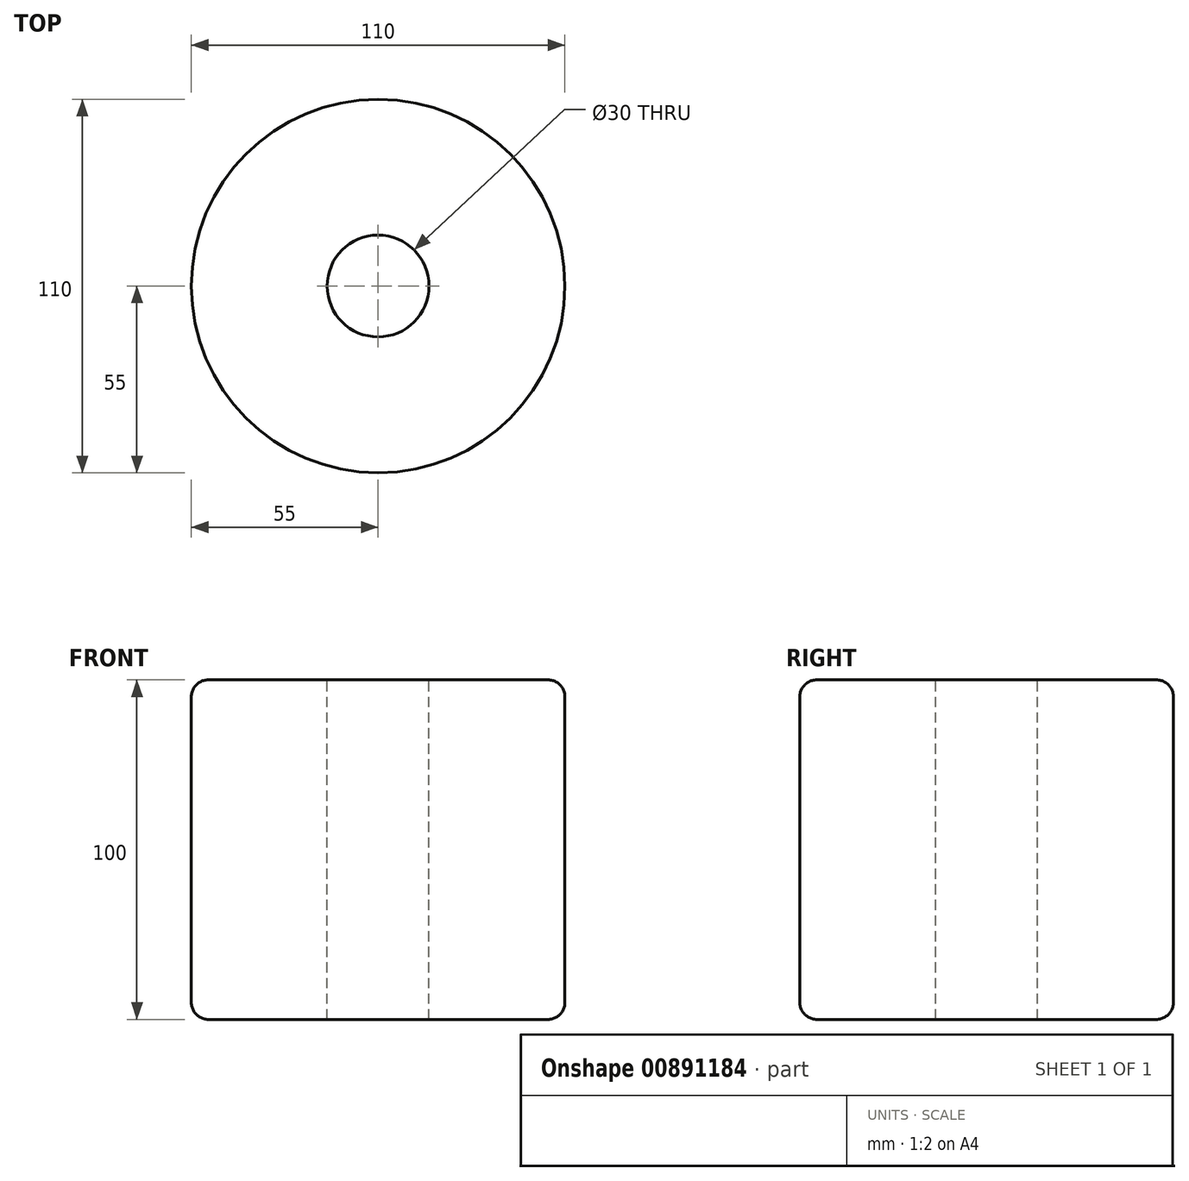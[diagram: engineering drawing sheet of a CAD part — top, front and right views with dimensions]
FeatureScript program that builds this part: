
annotation { "Feature Type Name" : "Feature", "Feature Type Description" : "" }
export const myFeature = defineFeature(function(context is Context, id is Id, definition is map)
    precondition{}
    {
        {
            var Q0;
            Q0=qCreatedBy(makeId("Front.planeOp"),FACE);
            var sketch = newSketch(context, id + "F0", { "sketchPlane" : qUnion([Q0])});
            skLineSegment(sketch, "E0", {"start": v(0, 66.21) * mm, "end": v(0, -56.82) * mm, "construction": true});
            skLineSegment(sketch, "E1.bottom", {"start": v(15, 50) * mm, "end": v(55, 50) * mm});
            skLineSegment(sketch, "E1.top", {"start": v(15, -50) * mm, "end": v(55, -50) * mm});
            skLineSegment(sketch, "E1.left", {"start": v(15, 50) * mm, "end": v(15, -50) * mm});
            skLineSegment(sketch, "E1.right", {"start": v(55, 50) * mm, "end": v(55, -50) * mm});
            skLineSegment(sketch, "E2", {"start": v(-74.72, 0) * mm, "end": v(76.46, 0) * mm, "construction": true});
            skSolve(sketch);
        }
        {
            var Q0;
            Q0=makeQuery(id+"F0.imprint","IMPRINT",FACE,{"disambiguationData":[TD([[makeQuery(id+"F0.imprint","IMPRINT",EDGE,{"derivedFrom":sQuery(id+"F0.wireOp",EDGE,"E1.bottom")}),-1.0]])]});
            var Q1;
            Q1=sQuery(id+"F0.wireOp",EDGE,"E0");
            revolve(context, id + "F1", {"surfaceOperationType" : NewSurfaceOperationType.NEW, "entities" : qUnion([Q0]), "axis" : qUnion([Q1]), "revolveType" : RevolveType.FULL});
        }
        {
            var Q0;
            Q0=makeQuery(id+"F1.opRevolve","SWEPT_EDGE",EDGE,{"disambiguationData":[OSD([sQuery(id+"F0.wireOp",EDGE,"E1.bottom"),sQuery(id+"F0.wireOp",EDGE,"E1.right")])]});
            var Q1;
            Q1=makeQuery(id+"F1.opRevolve","SWEPT_EDGE",EDGE,{"disambiguationData":[OSD([sQuery(id+"F0.wireOp",EDGE,"E1.top"),sQuery(id+"F0.wireOp",EDGE,"E1.right")])]});
            fillet(context, id + "F2", {"entities" : qUnion([Q0, Q1]), "radius" : 5 * mm, "tangentPropagation" : true, "allowEdgeOverflow" : false});
        }
    });
